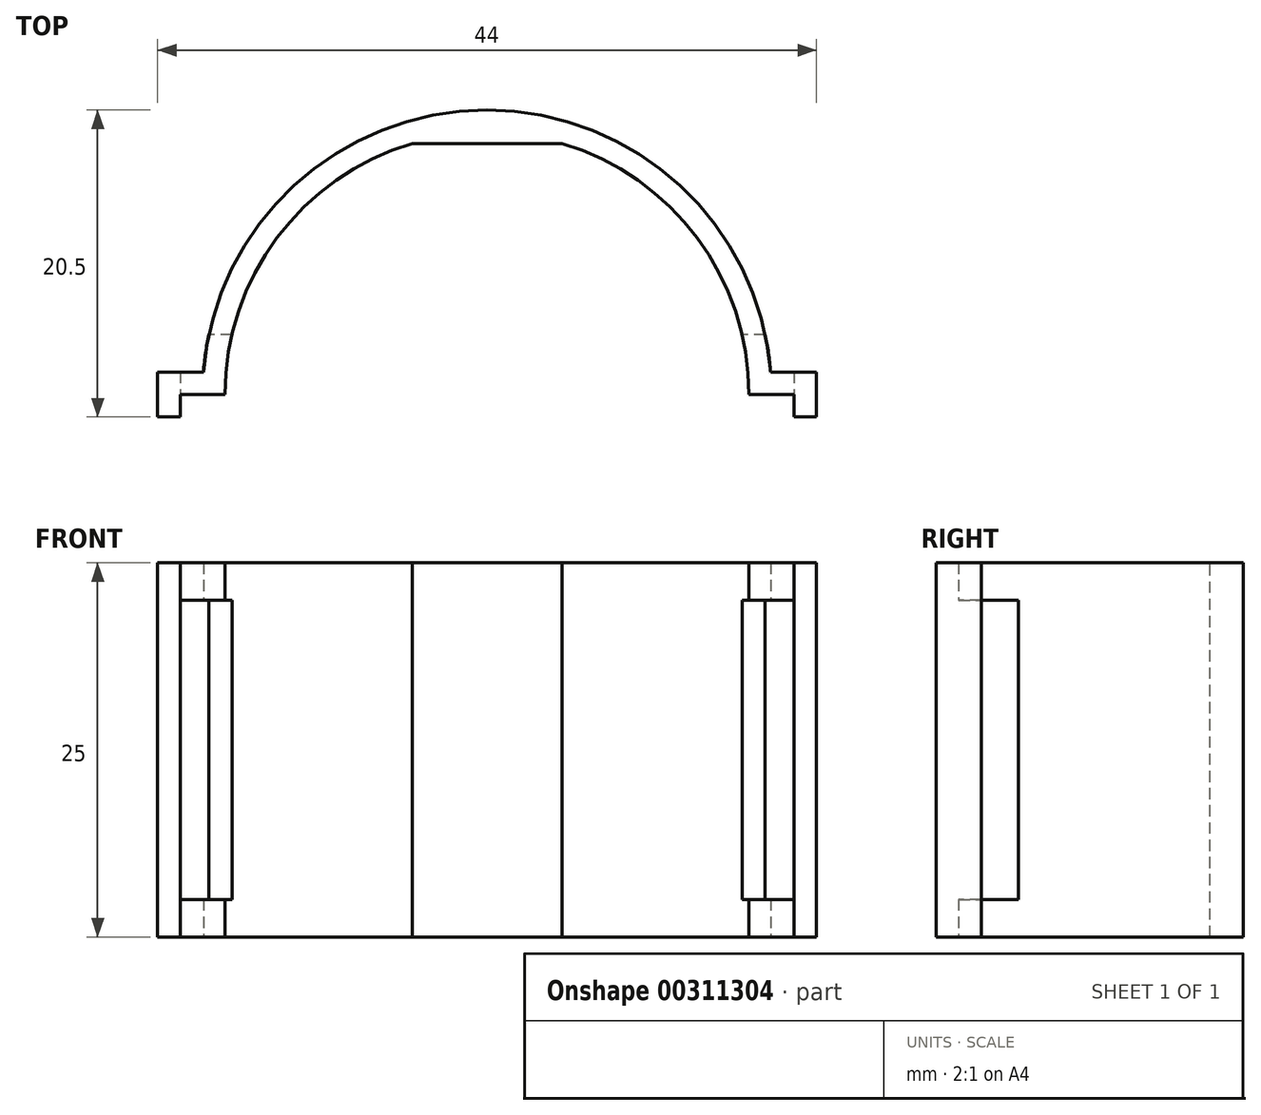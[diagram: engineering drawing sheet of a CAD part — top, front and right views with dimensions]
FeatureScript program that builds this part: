
annotation { "Feature Type Name" : "Feature", "Feature Type Description" : "" }
export const myFeature = defineFeature(function(context is Context, id is Id, definition is map)
    precondition{}
    {
        {
            var Q0;
            Q0=qCreatedBy(makeId("Top.planeOp"),FACE);
            var sketch = newSketch(context, id + "F0", { "sketchPlane" : qUnion([Q0])});
            skArc(sketch, "E0", {"start": v(17.5, 0) * mm, "mid": v(0, 17.5) * mm, "end": v(-17.5, 0) * mm});
            skArc(sketch, "E1", {"start": v(18.94, 1.5) * mm, "mid": v(0, 19) * mm, "end": v(-18.94, 1.5) * mm});
            skLineSegment(sketch, "E2", {"start": v(17.5, 0) * mm, "end": v(20.5, 0) * mm});
            skLineSegment(sketch, "E3", {"start": v(20.5, 0) * mm, "end": v(20.5, -1.5) * mm});
            skLineSegment(sketch, "E4", {"start": v(20.5, -1.5) * mm, "end": v(22, -1.5) * mm});
            skLineSegment(sketch, "E5", {"start": v(22, -1.5) * mm, "end": v(22, 1.5) * mm});
            skLineSegment(sketch, "E6", {"start": v(22, 1.5) * mm, "end": v(18.94, 1.5) * mm});
            skPoint(sketch, "E7.orphan", {"position": v(19, 0) * mm});
            skLineSegment(sketch, "E8", {"start": v(-17.5, 0) * mm, "end": v(-20.5, 0) * mm});
            skLineSegment(sketch, "E9", {"start": v(-20.5, 0) * mm, "end": v(-20.5, -1.5) * mm});
            skLineSegment(sketch, "E10", {"start": v(-20.5, -1.5) * mm, "end": v(-22, -1.5) * mm});
            skLineSegment(sketch, "E11", {"start": v(-22, -1.5) * mm, "end": v(-22, 1.5) * mm});
            skLineSegment(sketch, "E12", {"start": v(-22, 1.5) * mm, "end": v(-18.94, 1.5) * mm});
            skPoint(sketch, "E13.orphan", {"position": v(-19, 0) * mm});
            skSolve(sketch);
        }
        {
            var Q0;
            Q0 = qSketchRegion(id + "F0", true);
            extrude(context, id + "F1", {"entities" : qUnion([Q0]), "depth" : 25 * mm});
        }
        {
            var Q0;
            Q0=makeQuery(id+"F1.opExtrude","CAP_FACE",FACE,{"disambiguationData":[OSD([sQuery(id+"F0.wireOp",EDGE,"E0"),sQuery(id+"F0.wireOp",EDGE,"E1"),sQuery(id+"F0.wireOp",EDGE,"6q3Dvk6W-eCNe-GBYi-SmQf-hu2bjCXuBUmL"),sQuery(id+"F0.wireOp",EDGE,"MsS1NDyj-O8bH-DeNX-LdG3-79S3thxSg5Gj")])],"isStart":false});
            var sketch = newSketch(context, id + "F2", { "sketchPlane" : qUnion([Q0])});
            skArc(sketch, "E14", {"start": v(5, 18.33) * mm, "mid": v(0, 19) * mm, "end": v(-5, 18.33) * mm});
            skLineSegment(sketch, "E15", {"start": v(-5, 18.33) * mm, "end": v(-5, 16.77) * mm});
            skLineSegment(sketch, "E16", {"start": v(5, 16.77) * mm, "end": v(5, 18.33) * mm});
            skLineSegment(sketch, "E17", {"start": v(-5, 16.77) * mm, "end": v(5, 16.77) * mm});
            skSolve(sketch);
        }
        {
            var Q0;
            Q0 = qSketchRegion(id + "F2", true);
            extrude(context, id + "F3", {"entities" : qUnion([Q0]), "operationType" : NewBodyOperationType.ADD, "oppositeDirection" : true, "depth" : 25 * mm});
        }
        {
            var Q0;
            Q0=makeQuery(id+"F1.opExtrude","SWEPT_FACE",FACE,{"disambiguationData":[OSD([sQuery(id+"F0.wireOp",EDGE,"E8")])]});
            var sketch = newSketch(context, id + "F4", { "sketchPlane" : qUnion([Q0])});
            skLineSegment(sketch, "E18.bottom", {"start": v(20.5, 2.5) * mm, "end": v(-20.5, 2.5) * mm});
            skLineSegment(sketch, "E18.top", {"start": v(20.5, 22.5) * mm, "end": v(-20.5, 22.5) * mm});
            skLineSegment(sketch, "E18.left", {"start": v(20.5, 2.5) * mm, "end": v(20.5, 22.5) * mm});
            skLineSegment(sketch, "E18.right", {"start": v(-20.5, 2.5) * mm, "end": v(-20.5, 22.5) * mm});
            skSolve(sketch);
        }
        {
            var Q0;
            Q0 = qSketchRegion(id + "F4", true);
            extrude(context, id + "F5", {"entities" : qUnion([Q0]), "operationType" : NewBodyOperationType.REMOVE, "oppositeDirection" : true, "depth" : 4 * mm});
        }
    });
